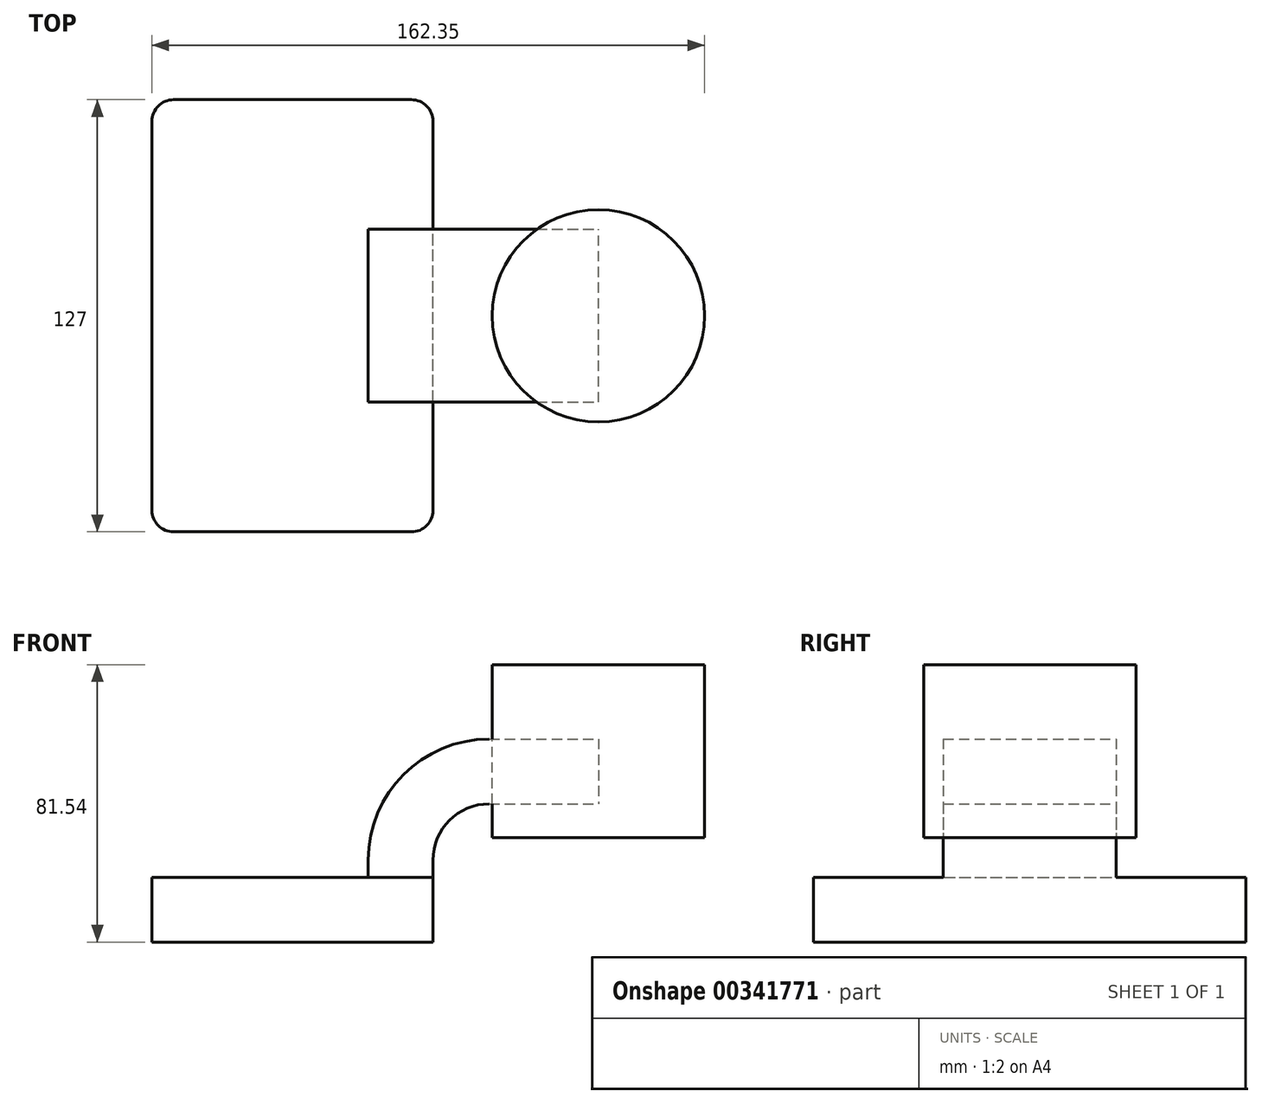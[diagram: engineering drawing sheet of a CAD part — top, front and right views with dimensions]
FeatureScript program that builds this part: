
annotation { "Feature Type Name" : "Feature", "Feature Type Description" : "" }
export const myFeature = defineFeature(function(context is Context, id is Id, definition is map)
    precondition{}
    {
        {
            var Q0;
            Q0=qCreatedBy(makeId("Front.planeOp"),FACE);
            var sketch = newSketch(context, id + "F0", { "sketchPlane" : qUnion([Q0])});
            skLineSegment(sketch, "E0.bottom", {"start": v(-41.28, 9.52) * mm, "end": v(41.28, 9.53) * mm});
            skLineSegment(sketch, "E0.top", {"start": v(-41.28, -9.52) * mm, "end": v(41.28, -9.52) * mm});
            skLineSegment(sketch, "E0.left", {"start": v(-41.28, 9.52) * mm, "end": v(-41.27, -9.53) * mm});
            skLineSegment(sketch, "E0.right", {"start": v(41.28, 9.53) * mm, "end": v(41.28, -9.52) * mm});
            skPoint(sketch, "E0.middle", {"position": v(0, 0) * mm});
            skLineSegment(sketch, "E1.bottom", {"start": v(70.28, 72) * mm, "end": v(121.08, 72) * mm});
            skLineSegment(sketch, "E1.top", {"start": v(70.28, 21.2) * mm, "end": v(121.08, 21.2) * mm});
            skLineSegment(sketch, "E1.left", {"start": v(70.28, 72) * mm, "end": v(70.28, 21.2) * mm});
            skLineSegment(sketch, "E1.right", {"start": v(121.08, 72) * mm, "end": v(121.08, 21.2) * mm});
            skPoint(sketch, "E1.middle", {"position": v(95.68, 46.6) * mm});
            skLineSegment(sketch, "E2", {"start": v(41.27, 9.53) * mm, "end": v(41.27, 14.57) * mm});
            skArc(sketch, "E3", {"start": v(41.28, 14.57) * mm, "mid": v(46.11, 26.24) * mm, "end": v(57.79, 31.08) * mm});
            skLineSegment(sketch, "E4", {"start": v(57.79, 31.08) * mm, "end": v(110.19, 31.08) * mm});
            skLineSegment(sketch, "E5.0", {"start": v(57.79, 50.13) * mm, "end": v(91.07, 50.13) * mm});
            skArc(sketch, "E5.1", {"start": v(22.23, 14.57) * mm, "mid": v(32.64, 39.71) * mm, "end": v(57.79, 50.13) * mm});
            skLineSegment(sketch, "E5.2", {"start": v(22.22, 9.53) * mm, "end": v(22.22, 14.57) * mm});
            skFitSpline(sketch, "E6", {"points": [v(-41.28, 9.52) * mm, v(57.79, 50.13) * mm], "startDerivative": vector(123.83, 30.28) * mm, "endDerivative": vector(151.15, -33.02) * mm});
            skLineSegment(sketch, "E7", {"start": v(89.88, 72) * mm, "end": v(89.88, 21.2) * mm});
            skSolve(sketch);
        }
        {
            var Q0;
            Q0=makeQuery(id+"F0.imprint","IMPRINT",FACE,{"disambiguationData":[TD([[makeQuery(id+"F0.imprint","IMPRINT",EDGE,{"derivedFrom":sQuery(id+"F0.wireOp",EDGE,"E0.top")}),1.0]])]});
            extrude(context, id + "F1", {"entities" : qUnion([Q0]), "depth" : 127 * mm, "symmetric" : true});
        }
        {
            var Q0;
            {var subQ1=sQuery(id+"F0.wireOp",EDGE,"E2");Q0=makeQuery(id+"F0.imprint","IMPRINT",FACE,{"disambiguationData":[TD([[makeQuery(id+"F0.imprint","IMPRINT",EDGE,{"derivedFrom":subQ1}),1.0]])]});}
            var Q1;
            {var subQ0=sQuery(id+"F0.wireOp",EDGE,"E5.0");var subQ1=sQuery(id+"F0.wireOp",EDGE,"E1.left");var subQ2=makeQuery(id+"F0.imprint","INTERSECT",VERTEX,{"derivedFrom":[subQ1,subQ0]});Q1=makeQuery(id+"F0.imprint","IMPRINT",FACE,{"disambiguationData":[TD([[makeQuery(id+"F0.imprint","IMPRINT",EDGE,{"disambiguationData":[TD([[subQ2,-1.0]])],"derivedFrom":subQ1}),1.0]])]});}
            extrude(context, id + "F2", {"entities" : qUnion([Q0, Q1]), "operationType" : NewBodyOperationType.ADD, "depth" : 50.8 * mm, "symmetric" : true});
        }
        {
            var Q0;
            Q0=makeQuery(id+"F0.imprint","IMPRINT",FACE,{"disambiguationData":[TD([[makeQuery(id+"F0.imprint","IMPRINT",EDGE,{"derivedFrom":sQuery(id+"F0.wireOp",EDGE,"E5.1")}),1.0]])]});
            extrude(context, id + "F3", {"entities" : qUnion([Q0]), "operationType" : NewBodyOperationType.ADD, "depth" : 15.88 * mm, "symmetric" : true});
        }
        {
            var Q0;
            {var subQ4=sQuery(id+"F0.wireOp",EDGE,"E1.right");Q0=makeQuery(id+"F0.imprint","IMPRINT",FACE,{"disambiguationData":[TD([[makeQuery(id+"F0.imprint","IMPRINT",EDGE,{"derivedFrom":subQ4}),-1.0]])]});}
            var Q1;
            Q1=sQuery(id+"F0.wireOp",EDGE,"E7");
            revolve(context, id + "F4", {"entities" : qUnion([Q0]), "axis" : qUnion([Q1]), "revolveType" : RevolveType.FULL});
        }
        {
            var Q0;
            Q0=makeQuery(id+"F1.opExtrude","CAP_EDGE",EDGE,{"disambiguationData":[OSD([sQuery(id+"F0.wireOp",EDGE,"E0.right")])],"isStart":false});
            var Q1;
            Q1=makeQuery(id+"F1.opExtrude","CAP_EDGE",EDGE,{"disambiguationData":[OSD([sQuery(id+"F0.wireOp",EDGE,"E0.left")])],"isStart":false});
            var Q2;
            Q2=makeQuery(id+"F1.opExtrude","CAP_EDGE",EDGE,{"disambiguationData":[OSD([sQuery(id+"F0.wireOp",EDGE,"E0.right")])],"isStart":true});
            var Q3;
            Q3=makeQuery(id+"F1.opExtrude","CAP_EDGE",EDGE,{"disambiguationData":[OSD([sQuery(id+"F0.wireOp",EDGE,"E0.left")])],"isStart":true});
            fillet(context, id + "F5", {"entities" : qUnion([Q0, Q1, Q2, Q3]), "radius" : 6.35 * mm, "tangentPropagation" : true, "allowEdgeOverflow" : false});
        }
    });
